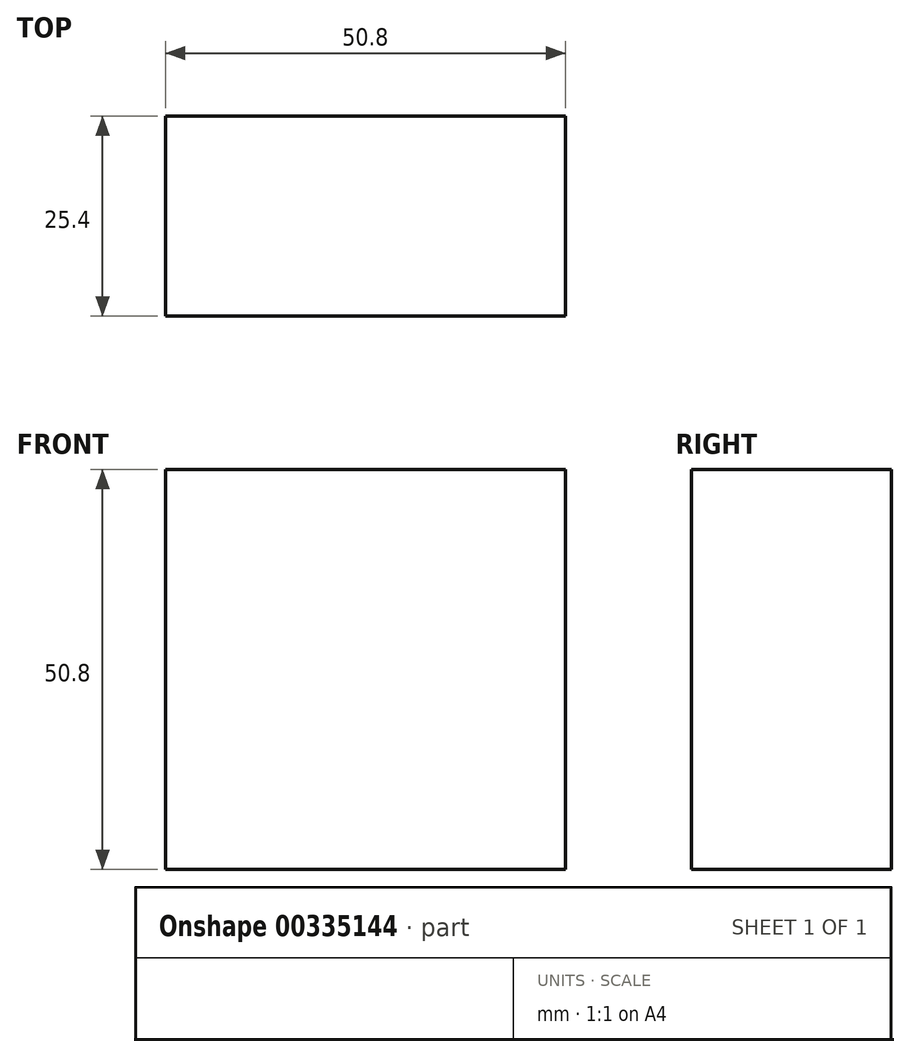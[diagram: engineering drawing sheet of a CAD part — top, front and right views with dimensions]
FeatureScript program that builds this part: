
annotation { "Feature Type Name" : "Feature", "Feature Type Description" : "" }
export const myFeature = defineFeature(function(context is Context, id is Id, definition is map)
    precondition{}
    {
        {
            var Q0;
            Q0=qCreatedBy(makeId("Front.planeOp"),FACE);
            var sketch = newSketch(context, id + "F0", { "sketchPlane" : qUnion([Q0])});
            skLineSegment(sketch, "E0.bottom", {"start": v(-31.4, 36.93) * mm, "end": v(19.4, 36.93) * mm});
            skLineSegment(sketch, "E0.top", {"start": v(-31.4, -13.87) * mm, "end": v(19.4, -13.87) * mm});
            skLineSegment(sketch, "E0.left", {"start": v(-31.4, 36.93) * mm, "end": v(-31.4, -13.87) * mm});
            skLineSegment(sketch, "E0.right", {"start": v(19.4, 36.93) * mm, "end": v(19.4, -13.87) * mm});
            skSolve(sketch);
        }
        {
            var Q0;
            Q0 = qSketchRegion(id + "F0", true);
            extrude(context, id + "F1", {"entities" : qUnion([Q0]), "depth" : 25.4 * mm});
        }
    });
